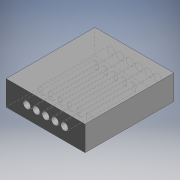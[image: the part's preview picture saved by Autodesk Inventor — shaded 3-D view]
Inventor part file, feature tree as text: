
AUTODESK INVENTOR PART (.ipt)
format: ipt  version: 2019 (Build 230136000, 136)  size: 126,976 bytes
history: native  units: mm (DEFAULTED — no unit token found)
features: sketch x2, hole x2, extrude x1
ambient origin geometry x8: Origin, YZ Plane, XZ Plane, XY Plane, X Axis, Y Axis, Z Axis, Center Point
bodies: Solid1 (feature_tree)
feature tree (5):
  sketch  "Sketch1"  dims[d0=0.0mm d1=57.15mm d2=57.15mm d3=0.0mm]
  sketch  "Sketch2"  dims[d4=4.7625mm d5=19.05mm d6=9.525mm d7=6.35mm d8=14.3117mm d9=44.499505mm d10=20.594885mm d11=4.7625mm d12=19.05mm d13=9.525mm d14=6.35mm d15=14.3117mm d16=44.499505mm d17=20.594885mm]
  extrude  "Extrusion1"  Depth=57.15mm TaperAngle=0.0deg
  hole  "Hole1"  [1 undecoded]
  hole  "Hole2"  [1 undecoded]
note: 2 required parameter values undecoded (feature->parameter linkage not recoverable at this tier; creation-order binding heuristic only, values carry confidence <= 0.55)
